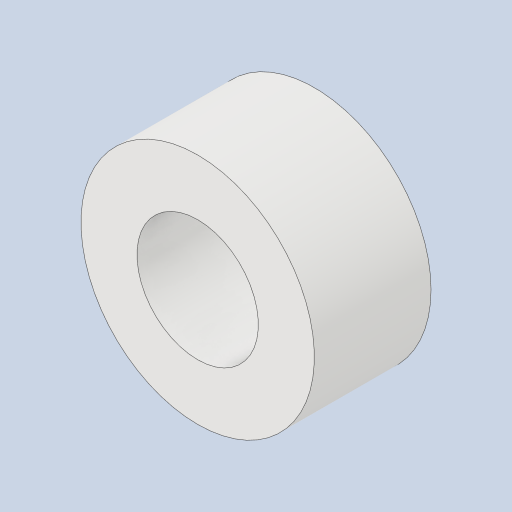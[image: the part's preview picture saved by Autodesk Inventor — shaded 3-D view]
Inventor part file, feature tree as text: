
AUTODESK INVENTOR PART (.ipt)
format: ipt  version: 2023 (Build 270158000, 158)  size: 135,168 bytes
history: native  units: mm
features: sketch x3, revolve x1, hole x1, extrude x1
ambient origin geometry x8: Origin, YZ Plane, XZ Plane, XY Plane, X Axis, Y Axis, Z Axis, Center Point
bodies: Solid1 (feature_tree)
feature tree (6):
  revolve  "Revolution1"  [1 undecoded]
  hole  "Hole1"  [1 undecoded]
  extrude  "押し出し1"  [1 undecoded]
  sketch  "Sketch_1"  dims[d0=360.0deg]
  sketch  "Sketch2"  dims[d1=2.6mm d2=6.0mm d3=4.0mm d4=2.0mm d5=90.0deg d6=4.5mm d7=0.0mm d8=2.0mm d9=0.0mm]
  sketch  "スケッチ3"
note: 3 required parameter values undecoded (feature->parameter linkage not recoverable at this tier; creation-order binding heuristic only, values carry confidence <= 0.55)